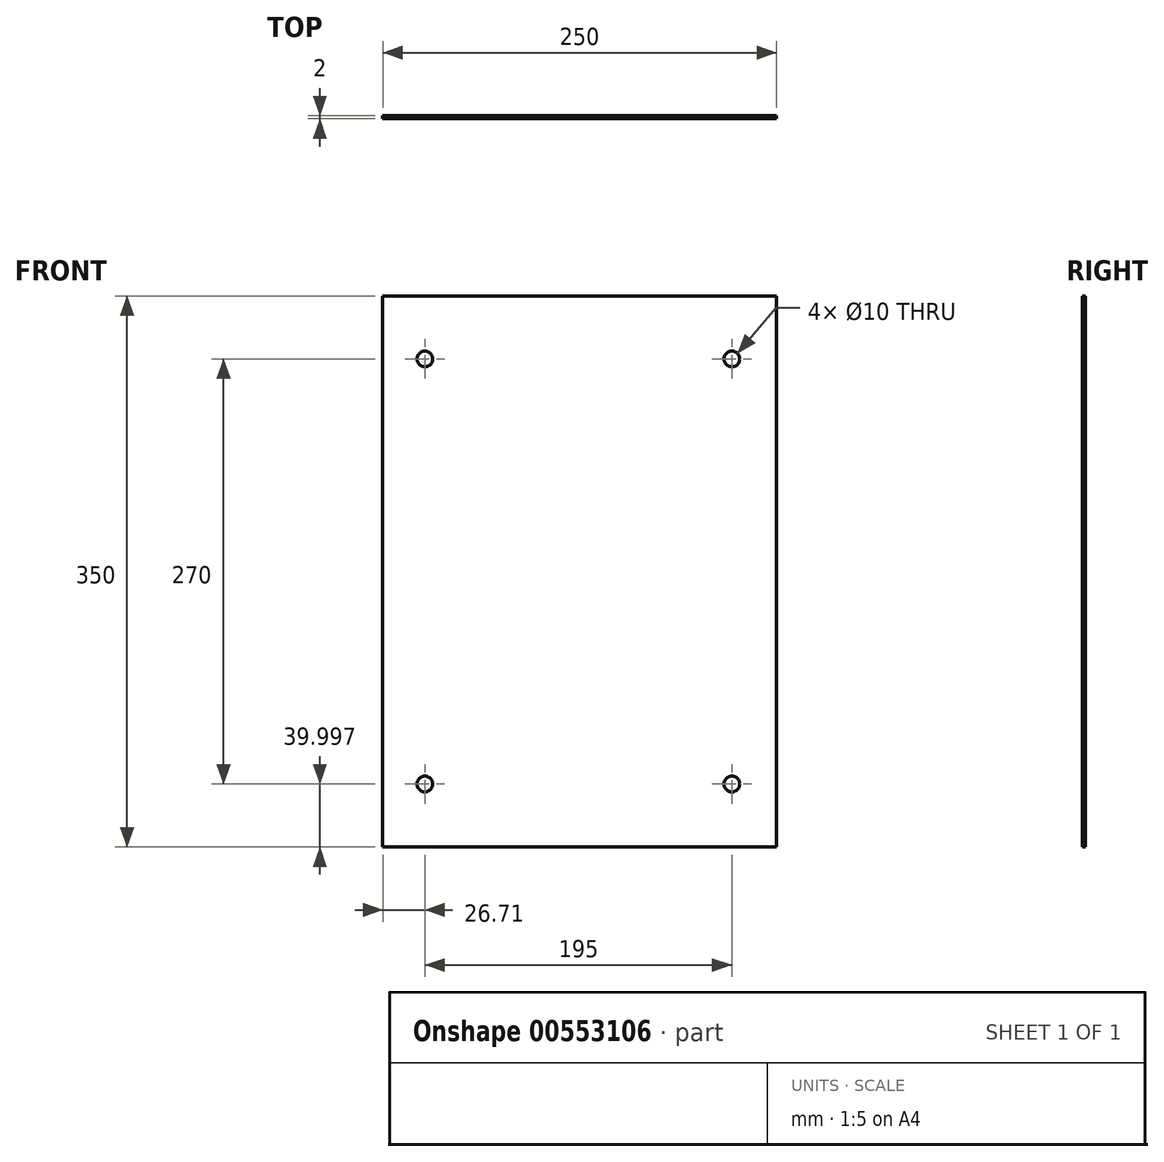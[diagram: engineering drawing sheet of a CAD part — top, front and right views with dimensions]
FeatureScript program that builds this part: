
annotation { "Feature Type Name" : "Feature", "Feature Type Description" : "" }
export const myFeature = defineFeature(function(context is Context, id is Id, definition is map)
    precondition{}
    {
        {
            var Q0;
            Q0=qCreatedBy(makeId("Front.planeOp"),FACE);
            var sketch = newSketch(context, id + "F0", { "sketchPlane" : qUnion([Q0])});
            skLineSegment(sketch, "E0.bottom", {"start": v(-124.21, 243.62) * mm, "end": v(125.79, 243.62) * mm});
            skLineSegment(sketch, "E0.top", {"start": v(-124.21, -106.38) * mm, "end": v(125.79, -106.38) * mm});
            skLineSegment(sketch, "E0.left", {"start": v(-124.21, 243.62) * mm, "end": v(-124.21, -106.38) * mm});
            skLineSegment(sketch, "E0.right", {"start": v(125.79, 243.62) * mm, "end": v(125.79, -106.38) * mm});
            skLineSegment(sketch, "E1", {"start": v(0, 243.62) * mm, "end": v(0, -106.38) * mm, "construction": true});
            skLineSegment(sketch, "E2", {"start": v(-124.21, 68.62) * mm, "end": v(125.79, 68.62) * mm, "construction": true});
            skLineSegment(sketch, "E3.bottom", {"start": v(-97.5, -66.38) * mm, "end": v(97.5, -66.38) * mm, "construction": true});
            skLineSegment(sketch, "E3.top", {"start": v(-97.5, 203.62) * mm, "end": v(97.5, 203.62) * mm, "construction": true});
            skLineSegment(sketch, "E3.left", {"start": v(-97.5, -66.38) * mm, "end": v(-97.5, 203.62) * mm, "construction": true});
            skLineSegment(sketch, "E3.right", {"start": v(97.5, -66.38) * mm, "end": v(97.5, 203.62) * mm, "construction": true});
            skPoint(sketch, "E3.middle", {"position": v(0, 68.62) * mm});
            skCircle(sketch, "E4", {"center": v(-97.5, -66.38) * mm, "radius": 5 * mm});
            skCircle(sketch, "E5", {"center": v(97.5, -66.38) * mm, "radius": 5 * mm});
            skCircle(sketch, "E6", {"center": v(-97.5, 203.62) * mm, "radius": 5 * mm});
            skCircle(sketch, "E7", {"center": v(97.5, 203.62) * mm, "radius": 5 * mm});
            skSolve(sketch);
        }
        {
            var Q0;
            Q0 = qSketchRegion(id + "F0", true);
            extrude(context, id + "F1", {"entities" : qUnion([Q0]), "depth" : 2 * mm, "offsetDistance" : 25 * mm});
        }
    });
